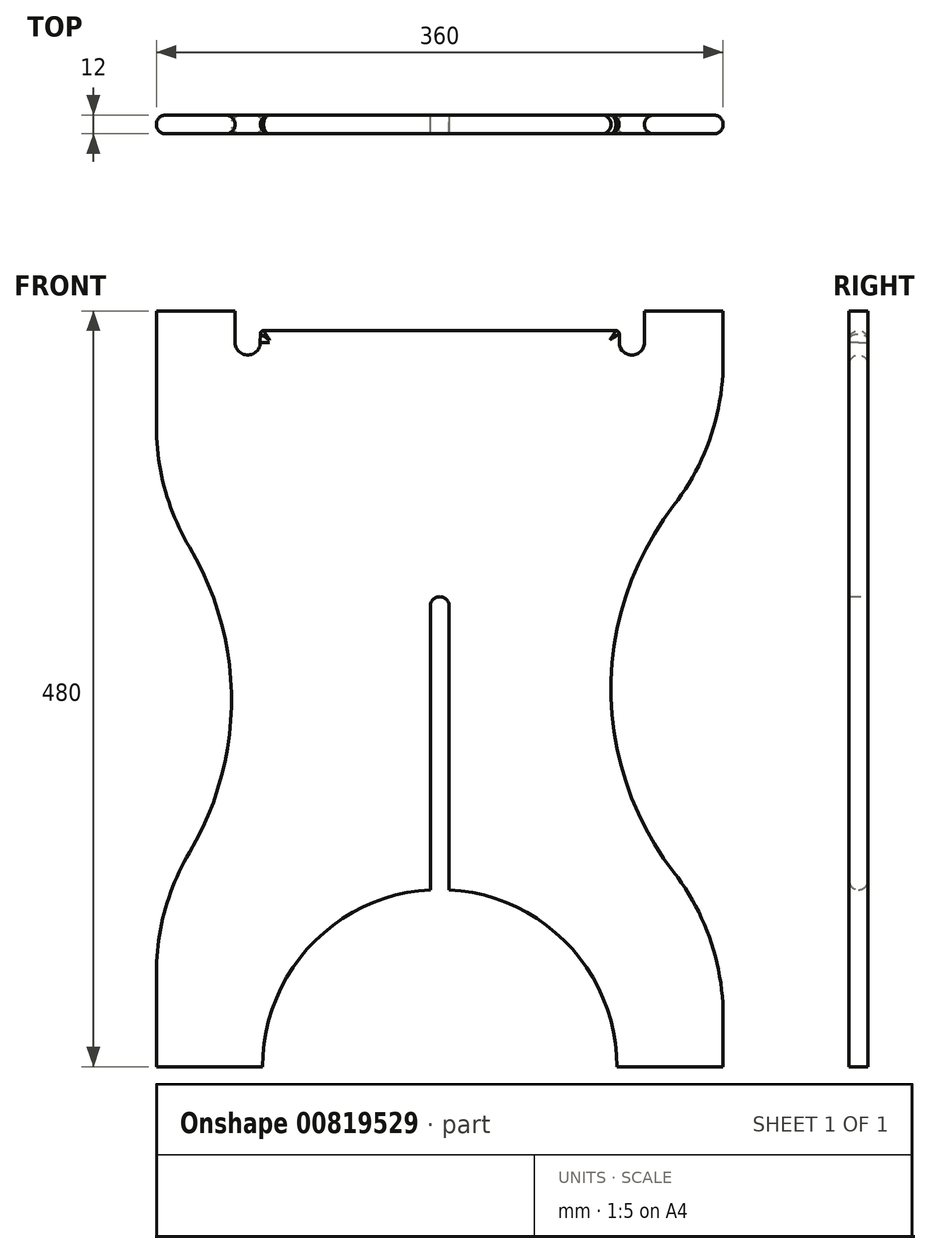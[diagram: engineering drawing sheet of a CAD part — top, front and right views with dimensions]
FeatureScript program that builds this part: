
annotation { "Feature Type Name" : "Feature", "Feature Type Description" : "" }
export const myFeature = defineFeature(function(context is Context, id is Id, definition is map)
    precondition{}
    {
        {
            var Q0;
            Q0=qCreatedBy(makeId("Front.planeOp"),FACE);
            var sketch = newSketch(context, id + "F0", { "sketchPlane" : qUnion([Q0])});
            skLineSegment(sketch, "E0.bottom", {"start": v(-180, -240) * mm, "end": v(-112.5, -240) * mm});
            skLineSegment(sketch, "E0.top", {"start": v(-180, 240) * mm, "end": v(-130, 240) * mm});
            skLineSegment(sketch, "E0.left", {"start": v(-180, -240) * mm, "end": v(-180, -180.56) * mm});
            skLineSegment(sketch, "E0.right", {"start": v(180, -240) * mm, "end": v(180, -208.23) * mm});
            skPoint(sketch, "E0.middle", {"position": v(0, 0) * mm});
            skLineSegment(sketch, "E1.0", {"start": v(-130, 228) * mm, "end": v(-130, 240) * mm});
            skLineSegment(sketch, "E2.0", {"start": v(130, 227.51) * mm, "end": v(130, 240) * mm});
            skLineSegment(sketch, "E3.trimOffspring", {"start": v(130, 240) * mm, "end": v(180, 240) * mm});
            skArc(sketch, "E4", {"start": v(112.5, -240) * mm, "mid": v(81.64, -162.6) * mm, "end": v(6, -127.66) * mm});
            skLineSegment(sketch, "E5.trimOffspring", {"start": v(112.5, -240) * mm, "end": v(180, -240) * mm});
            skArc(sketch, "E6", {"start": v(148.58, 116.36) * mm, "mid": v(108.78, 0) * mm, "end": v(148.58, -116.36) * mm});
            skArc(sketch, "E7", {"start": v(-158.98, -103.98) * mm, "mid": v(-132.35, -6.97) * mm, "end": v(-158.98, 90.04) * mm});
            skLineSegment(sketch, "E8.trimOffspring", {"start": v(-180, 166.62) * mm, "end": v(-180, 240) * mm});
            skLineSegment(sketch, "E9.trimOffspring", {"start": v(180, 208.23) * mm, "end": v(180, 240) * mm});
            skPoint(sketch, "E10.visualSharp", {"position": v(-180, 118.88) * mm});
            skArc(sketch, "E10.filletArc", {"start": v(-180, 166.62) * mm, "mid": v(-174.65, 126.91) * mm, "end": v(-158.98, 90.04) * mm});
            skPoint(sketch, "E11.visualSharp", {"position": v(-180, -132.82) * mm});
            skArc(sketch, "E11.filletArc", {"start": v(-158.98, -103.98) * mm, "mid": v(-174.65, -140.85) * mm, "end": v(-180, -180.56) * mm});
            skPoint(sketch, "E12.visualSharp", {"position": v(180, 148.3) * mm});
            skArc(sketch, "E12.filletArc", {"start": v(148.58, 116.36) * mm, "mid": v(171.93, 159.68) * mm, "end": v(180, 208.23) * mm});
            skPoint(sketch, "E13.visualSharp", {"position": v(180, -148.3) * mm});
            skArc(sketch, "E13.filletArc", {"start": v(180, -208.23) * mm, "mid": v(171.93, -159.68) * mm, "end": v(148.58, -116.36) * mm});
            skArc(sketch, "E14", {"start": v(114, 220) * mm, "mid": v(122, 212) * mm, "end": v(130, 220) * mm});
            skArc(sketch, "E15", {"start": v(-130, 220) * mm, "mid": v(-122, 212) * mm, "end": v(-114, 220) * mm});
            skLineSegment(sketch, "E16", {"start": v(-130, 228) * mm, "end": v(-130, 220) * mm});
            skLineSegment(sketch, "E17", {"start": v(-114, 220) * mm, "end": v(-113.99, 225.5) * mm});
            skLineSegment(sketch, "E18.trimOffspring", {"start": v(-111.99, 227.5) * mm, "end": v(112, 227.5) * mm});
            skLineSegment(sketch, "E19", {"start": v(130, 227.51) * mm, "end": v(130, 220) * mm});
            skLineSegment(sketch, "E20", {"start": v(114, 220) * mm, "end": v(114, 225.5) * mm});
            skPoint(sketch, "E21.visualSharp", {"position": v(-113.98, 227.5) * mm});
            skArc(sketch, "E21.filletArc", {"start": v(-111.99, 227.5) * mm, "mid": v(-113.4, 226.9) * mm, "end": v(-113.99, 225.5) * mm});
            skPoint(sketch, "E22.visualSharp", {"position": v(114, 227.5) * mm});
            skArc(sketch, "E22.filletArc", {"start": v(114, 225.5) * mm, "mid": v(113.41, 226.92) * mm, "end": v(112, 227.5) * mm});
            skLineSegment(sketch, "E23.0", {"start": v(6, -127.66) * mm, "end": v(6, 52.5) * mm});
            skLineSegment(sketch, "E24.0", {"start": v(-6, -127.66) * mm, "end": v(-6, 52.5) * mm});
            skArc(sketch, "E25", {"start": v(6, 52.5) * mm, "mid": v(0, 58.5) * mm, "end": v(-6, 52.5) * mm});
            skArc(sketch, "E26.trimOffspring", {"start": v(-6, -127.66) * mm, "mid": v(-81.64, -162.6) * mm, "end": v(-112.5, -240) * mm});
            skSolve(sketch);
        }
        {
            var Q0;
            Q0=makeQuery(id+"F0.imprint","IMPRINT",FACE,{"disambiguationData":[TD([[makeQuery(id+"F0.imprint","IMPRINT",EDGE,{"derivedFrom":sQuery(id+"F0.wireOp",EDGE,"E0.bottom")}),1.0]])]});
            extrude(context, id + "F1", {"entities" : qUnion([Q0]), "endBound" : BoundingType.SYMMETRIC, "depth" : 12 * mm, "offsetDistance" : 25 * mm});
        }
        {
            var Q0;
            Q0=makeQuery(id+"F1.opExtrude","CAP_EDGE",EDGE,{"disambiguationData":[OSD([sQuery(id+"F0.wireOp",EDGE,"E0.right")])],"isStart":false});
            var Q1;
            Q1=makeQuery(id+"F1.opExtrude","CAP_EDGE",EDGE,{"disambiguationData":[OSD([sQuery(id+"F0.wireOp",EDGE,"E0.right")])],"isStart":true});
            var Q2;
            Q2=makeQuery(id+"F1.opExtrude","CAP_EDGE",EDGE,{"disambiguationData":[OSD([sQuery(id+"F0.wireOp",EDGE,"E0.left")])],"isStart":false});
            var Q3;
            Q3=makeQuery(id+"F1.opExtrude","CAP_EDGE",EDGE,{"disambiguationData":[OSD([sQuery(id+"F0.wireOp",EDGE,"E0.left")])],"isStart":true});
            var Q4;
            Q4=makeQuery(id+"F1.opExtrude","CAP_EDGE",EDGE,{"disambiguationData":[OSD([sQuery(id+"F0.wireOp",EDGE,"E4")])],"isStart":false});
            var Q5;
            Q5=makeQuery(id+"F1.opExtrude","CAP_EDGE",EDGE,{"disambiguationData":[OSD([sQuery(id+"F0.wireOp",EDGE,"E4")])],"isStart":true});
            var Q6;
            Q6=makeQuery(id+"F1.opExtrude","CAP_EDGE",EDGE,{"disambiguationData":[OSD([sQuery(id+"F0.wireOp",EDGE,"E26.trimOffspring")])],"isStart":false});
            var Q7;
            Q7=makeQuery(id+"F1.opExtrude","CAP_EDGE",EDGE,{"disambiguationData":[OSD([sQuery(id+"F0.wireOp",EDGE,"E26.trimOffspring")])],"isStart":true});
            var Q8;
            Q8=makeQuery(id+"F1.opExtrude","CAP_EDGE",EDGE,{"disambiguationData":[OSD([sQuery(id+"F0.wireOp",EDGE,"E2.0"),sQuery(id+"F0.wireOp",EDGE,"E19")])],"isStart":false});
            var Q9;
            Q9=makeQuery(id+"F1.opExtrude","CAP_EDGE",EDGE,{"disambiguationData":[OSD([sQuery(id+"F0.wireOp",EDGE,"E2.0"),sQuery(id+"F0.wireOp",EDGE,"E19")])],"isStart":true});
            var Q10;
            Q10=makeQuery(id+"F1.opExtrude","CAP_EDGE",EDGE,{"disambiguationData":[OSD([sQuery(id+"F0.wireOp",EDGE,"E1.0"),sQuery(id+"F0.wireOp",EDGE,"E16")])],"isStart":false});
            var Q11;
            Q11=makeQuery(id+"F1.opExtrude","CAP_EDGE",EDGE,{"disambiguationData":[OSD([sQuery(id+"F0.wireOp",EDGE,"E1.0"),sQuery(id+"F0.wireOp",EDGE,"E16")])],"isStart":true});
            fillet(context, id + "F2", {"entities" : qUnion([Q0, Q1, Q2, Q3, Q4, Q5, Q6, Q7, Q8, Q9, Q10, Q11]), "radius" : 6 * mm, "tangentPropagation" : true, "allowEdgeOverflow" : false});
        }
    });
